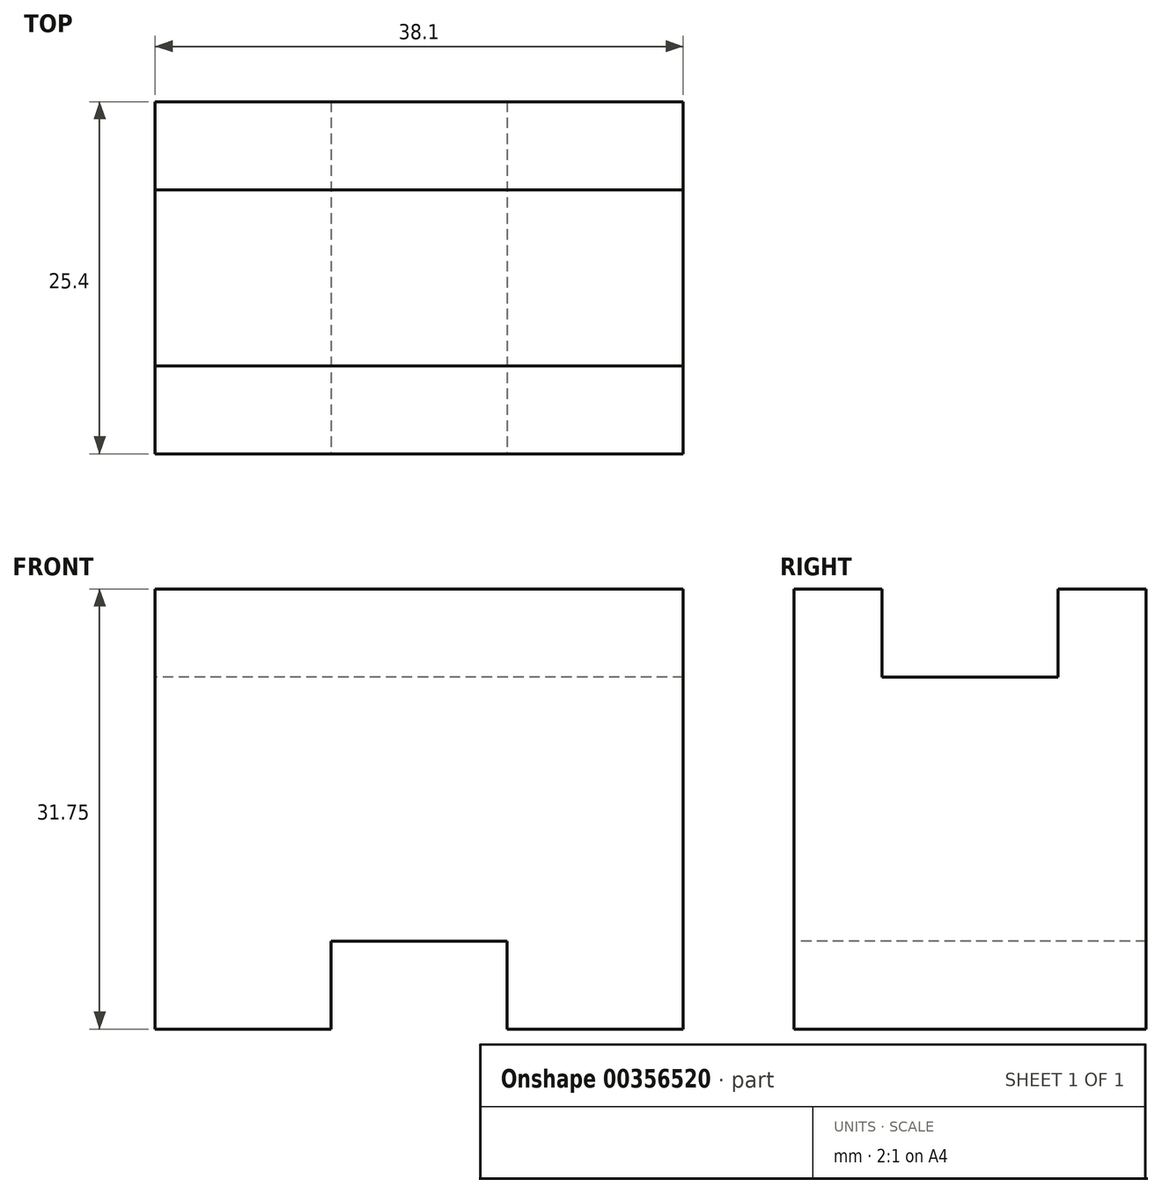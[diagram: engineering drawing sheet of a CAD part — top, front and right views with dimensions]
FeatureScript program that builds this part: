
annotation { "Feature Type Name" : "Feature", "Feature Type Description" : "" }
export const myFeature = defineFeature(function(context is Context, id is Id, definition is map)
    precondition{}
    {
        {
            var Q0;
            Q0=qCreatedBy(makeId("Right.planeOp"),FACE);
            var sketch = newSketch(context, id + "F0", { "sketchPlane" : qUnion([Q0])});
            skLineSegment(sketch, "E0", {"start": v(0, 0) * mm, "end": v(0, 31.75) * mm});
            skLineSegment(sketch, "E1", {"start": v(0, 31.75) * mm, "end": v(6.35, 31.75) * mm});
            skLineSegment(sketch, "E2", {"start": v(6.35, 31.75) * mm, "end": v(6.35, 25.4) * mm});
            skLineSegment(sketch, "E3", {"start": v(6.35, 25.4) * mm, "end": v(19.05, 25.4) * mm});
            skLineSegment(sketch, "E4", {"start": v(19.05, 25.4) * mm, "end": v(19.05, 31.75) * mm});
            skLineSegment(sketch, "E5", {"start": v(19.05, 31.75) * mm, "end": v(25.4, 31.75) * mm});
            skLineSegment(sketch, "E6", {"start": v(25.4, 31.75) * mm, "end": v(25.4, 0) * mm});
            skLineSegment(sketch, "E7", {"start": v(25.4, 0) * mm, "end": v(0, 0) * mm});
            skSolve(sketch);
        }
        {
            var Q0;
            Q0 = qSketchRegion(id + "F0", true);
            extrude(context, id + "F1", {"entities" : qUnion([Q0]), "depth" : 38.1 * mm});
        }
        {
            var Q0;
            Q0=makeQuery(id+"F1.opExtrude","SWEPT_FACE",FACE,{"disambiguationData":[OSD([sQuery(id+"F0.wireOp",EDGE,"E0")])]});
            var sketch = newSketch(context, id + "F2", { "sketchPlane" : qUnion([Q0])});
            skLineSegment(sketch, "E8", {"start": v(0, 0) * mm, "end": v(12.7, 0) * mm});
            skLineSegment(sketch, "E9", {"start": v(12.7, 0) * mm, "end": v(12.7, 6.35) * mm});
            skLineSegment(sketch, "E10", {"start": v(12.7, 6.35) * mm, "end": v(25.4, 6.35) * mm});
            skLineSegment(sketch, "E11", {"start": v(25.4, 6.35) * mm, "end": v(25.4, 0) * mm});
            skLineSegment(sketch, "E12", {"start": v(25.4, 0) * mm, "end": v(12.7, 0) * mm});
            skSolve(sketch);
        }
        {
            var Q0;
            Q0=makeQuery(id+"F2.imprint","IMPRINT",FACE,{"disambiguationData":[TD([[makeQuery(id+"F2.imprint","IMPRINT",EDGE,{"derivedFrom":sQuery(id+"F2.wireOp",EDGE,"E9")}),-1.0]])]});
            extrude(context, id + "F3", {"entities" : qUnion([Q0]), "operationType" : NewBodyOperationType.REMOVE, "oppositeDirection" : true, "depth" : 25.4 * mm});
        }
    });
